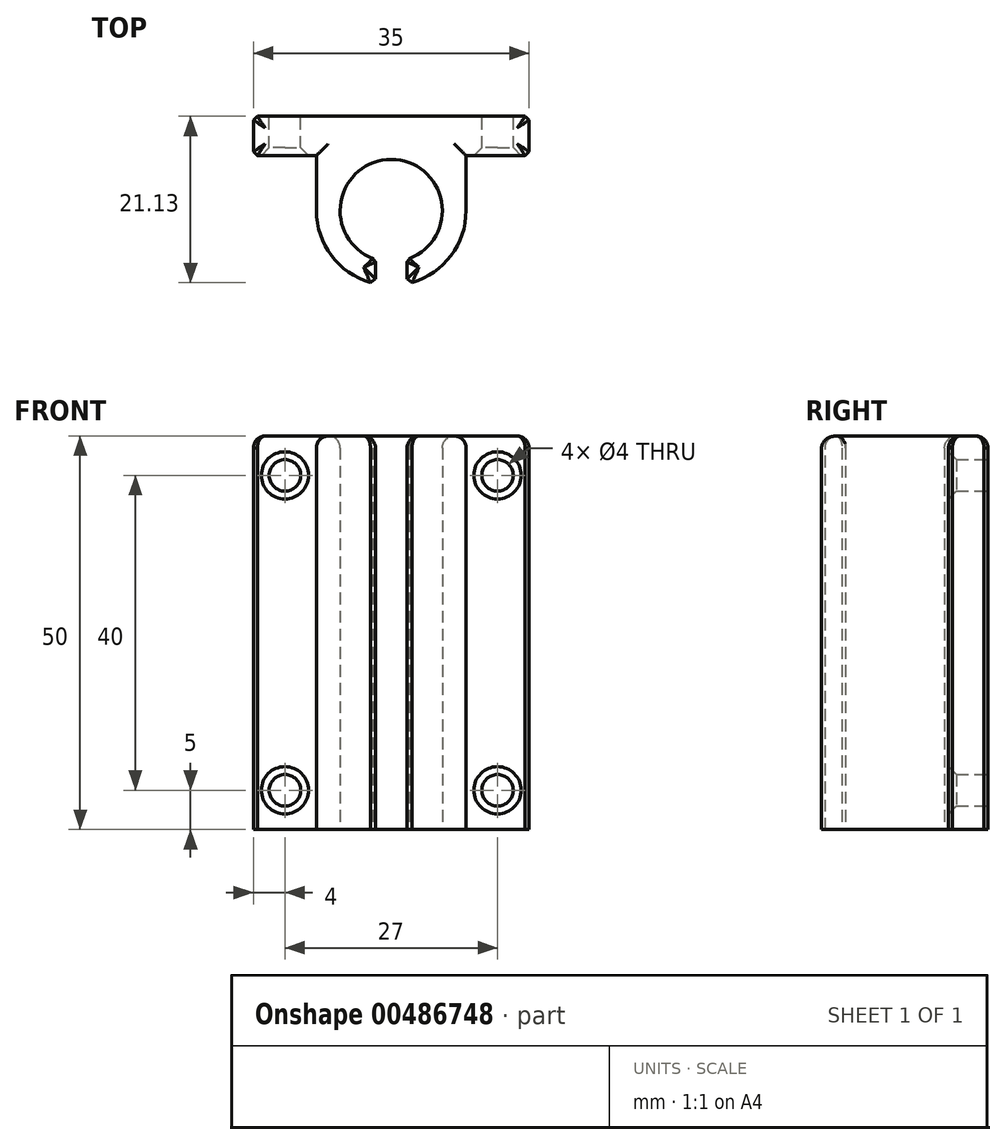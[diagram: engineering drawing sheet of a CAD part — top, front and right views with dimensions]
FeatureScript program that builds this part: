
annotation { "Feature Type Name" : "Feature", "Feature Type Description" : "" }
export const myFeature = defineFeature(function(context is Context, id is Id, definition is map)
    precondition{}
    {
        {
            var Q0;
            Q0=qCreatedBy(makeId("Top.planeOp"),FACE);
            var sketch = newSketch(context, id + "F0", { "sketchPlane" : qUnion([Q0])});
            skArc(sketch, "E0", {"start": v(2, -6.18) * mm, "mid": v(0, 6.5) * mm, "end": v(-2, -6.18) * mm});
            skArc(sketch, "E1", {"start": v(2, -9.29) * mm, "mid": v(7.4, -5.97) * mm, "end": v(9.5, 0) * mm});
            skLineSegment(sketch, "E2.0", {"start": v(-2, -6.18) * mm, "end": v(-2, -9.29) * mm});
            skLineSegment(sketch, "E3.0", {"start": v(2, -6.18) * mm, "end": v(2, -9.29) * mm});
            skLineSegment(sketch, "E4.bottom", {"start": v(17.5, 12) * mm, "end": v(-17.5, 12) * mm});
            skLineSegment(sketch, "E4.top", {"start": v(17.5, 7) * mm, "end": v(-17.5, 7) * mm});
            skLineSegment(sketch, "E4.left", {"start": v(17.5, 12) * mm, "end": v(17.5, 7) * mm});
            skLineSegment(sketch, "E4.right", {"start": v(-17.5, 12) * mm, "end": v(-17.5, 7) * mm});
            skPoint(sketch, "E4.middle", {"position": v(0, 9.5) * mm});
            skLineSegment(sketch, "E5", {"start": v(-9.5, 0) * mm, "end": v(-9.5, 7) * mm});
            skLineSegment(sketch, "E6", {"start": v(9.5, 0) * mm, "end": v(9.5, 7) * mm});
            skArc(sketch, "E7.trimOffspring", {"start": v(-9.5, 0) * mm, "mid": v(-7.4, -5.97) * mm, "end": v(-2, -9.29) * mm});
            skSolve(sketch);
        }
        {
            var Q0;
            Q0=makeQuery(id+"F0.imprint","IMPRINT",FACE,{"disambiguationData":[TD([[makeQuery(id+"F0.imprint","IMPRINT",EDGE,{"derivedFrom":sQuery(id+"F0.wireOp",EDGE,"E0")}),-1.0]])]});
            var Q1;
            Q1=makeQuery(id+"F0.imprint","IMPRINT",FACE,{"disambiguationData":[TD([[makeQuery(id+"F0.imprint","IMPRINT",EDGE,{"derivedFrom":sQuery(id+"F0.wireOp",EDGE,"E4.bottom")}),1.0]])]});
            extrude(context, id + "F1", {"entities" : qUnion([Q0, Q1]), "depth" : 50 * mm});
        }
        {
            var Q0;
            Q0=makeQuery(id+"F1.opExtrude","SWEPT_FACE",FACE,{"disambiguationData":[OSD([sQuery(id+"F0.wireOp",EDGE,"E4.bottom")])]});
            var sketch = newSketch(context, id + "F2", { "sketchPlane" : qUnion([Q0])});
            skCircle(sketch, "E8", {"center": v(13.5, 45) * mm, "radius": 2 * mm});
            skLineSegment(sketch, "E9", {"start": v(0, 50) * mm, "end": v(0, 0) * mm, "construction": true});
            skLineSegment(sketch, "E10", {"start": v(17.5, 25) * mm, "end": v(-17.5, 25) * mm, "construction": true});
            skCircle(sketch, "E11.MirrorC", {"center": v(-13.5, 45) * mm, "radius": 2 * mm});
            skCircle(sketch, "E12.MirrorC", {"center": v(-13.5, 5) * mm, "radius": 2 * mm});
            skCircle(sketch, "E13.MirrorC", {"center": v(13.5, 5) * mm, "radius": 2 * mm});
            skSolve(sketch);
        }
        {
            var Q0;
            Q0 = qSketchRegion(id + "F2", true);
            extrude(context, id + "F3", {"entities" : qUnion([Q0]), "operationType" : NewBodyOperationType.REMOVE, "endBound" : BoundingType.THROUGH_ALL, "oppositeDirection" : true, "depth" : 25 * mm});
        }
        {
            var Q0;
            {var subQ0=sQuery(id+"F0.wireOp",EDGE,"E4.top");Q0=makeQuery(id+"F3.boolean.opBoolean","INTERSECT",EDGE,{"derivedFrom":[makeQuery(id+"F1.opExtrude","SWEPT_FACE",FACE,{"disambiguationData":[OSD([subQ0]),TDD([makeQuery(id+"F0.imprint","IMPRINT",EDGE,{"disambiguationData":[TD([[makeQuery(id+"F0.imprint","INTERSECT",VERTEX,{"derivedFrom":[subQ0,sQuery(id+"F0.wireOp",EDGE,"E4.right")]}),1.0]])],"derivedFrom":subQ0})])]}),makeQuery(id+"F3.opExtrude","SWEPT_FACE",FACE,{"disambiguationData":[OSD([sQuery(id+"F2.wireOp",EDGE,"E8")])]})]});}
            var Q1;
            {var subQ0=sQuery(id+"F0.wireOp",EDGE,"E4.top");Q1=makeQuery(id+"F3.boolean.opBoolean","INTERSECT",EDGE,{"derivedFrom":[makeQuery(id+"F1.opExtrude","SWEPT_FACE",FACE,{"disambiguationData":[OSD([subQ0]),TDD([makeQuery(id+"F0.imprint","IMPRINT",EDGE,{"disambiguationData":[TD([[makeQuery(id+"F0.imprint","INTERSECT",VERTEX,{"derivedFrom":[subQ0,sQuery(id+"F0.wireOp",EDGE,"E4.left")]}),-1.0]])],"derivedFrom":subQ0})])]}),makeQuery(id+"F3.opExtrude","SWEPT_FACE",FACE,{"disambiguationData":[OSD([sQuery(id+"F2.wireOp",EDGE,"E11.MirrorC")])]})]});}
            var Q2;
            {var subQ0=sQuery(id+"F0.wireOp",EDGE,"E4.top");Q2=makeQuery(id+"F3.boolean.opBoolean","INTERSECT",EDGE,{"derivedFrom":[makeQuery(id+"F1.opExtrude","SWEPT_FACE",FACE,{"disambiguationData":[OSD([subQ0]),TDD([makeQuery(id+"F0.imprint","IMPRINT",EDGE,{"disambiguationData":[TD([[makeQuery(id+"F0.imprint","INTERSECT",VERTEX,{"derivedFrom":[subQ0,sQuery(id+"F0.wireOp",EDGE,"E4.left")]}),-1.0]])],"derivedFrom":subQ0})])]}),makeQuery(id+"F3.opExtrude","SWEPT_FACE",FACE,{"disambiguationData":[OSD([sQuery(id+"F2.wireOp",EDGE,"E12.MirrorC")])]})]});}
            var Q3;
            {var subQ0=sQuery(id+"F0.wireOp",EDGE,"E4.top");Q3=makeQuery(id+"F3.boolean.opBoolean","INTERSECT",EDGE,{"derivedFrom":[makeQuery(id+"F1.opExtrude","SWEPT_FACE",FACE,{"disambiguationData":[OSD([subQ0]),TDD([makeQuery(id+"F0.imprint","IMPRINT",EDGE,{"disambiguationData":[TD([[makeQuery(id+"F0.imprint","INTERSECT",VERTEX,{"derivedFrom":[subQ0,sQuery(id+"F0.wireOp",EDGE,"E4.right")]}),1.0]])],"derivedFrom":subQ0})])]}),makeQuery(id+"F3.opExtrude","SWEPT_FACE",FACE,{"disambiguationData":[OSD([sQuery(id+"F2.wireOp",EDGE,"E13.MirrorC")])]})]});}
            chamfer(context, id + "F4", {"entities" : qUnion([Q0, Q1, Q2, Q3]), "width" : 1 * mm, "tangentPropagation" : true});
        }
        {
            var Q0;
            Q0=makeQuery(id+"F1.opExtrude","CAP_FACE",FACE,{"disambiguationData":[OSD([sQuery(id+"F0.wireOp",EDGE,"E0"),sQuery(id+"F0.wireOp",EDGE,"E1"),sQuery(id+"F0.wireOp",EDGE,"E2.0"),sQuery(id+"F0.wireOp",EDGE,"E3.0"),sQuery(id+"F0.wireOp",EDGE,"E4.bottom"),sQuery(id+"F0.wireOp",EDGE,"E4.top"),sQuery(id+"F0.wireOp",EDGE,"E4.left"),sQuery(id+"F0.wireOp",EDGE,"E4.right"),sQuery(id+"F0.wireOp",EDGE,"E5"),sQuery(id+"F0.wireOp",EDGE,"E6"),sQuery(id+"F0.wireOp",EDGE,"E7.trimOffspring")])],"isStart":false});
            fillet(context, id + "F5", {"entities" : qUnion([Q0]), "radius" : 1.5 * mm, "tangentPropagation" : true, "allowEdgeOverflow" : false});
        }
        {
            var Q0;
            Q0=makeQuery(id+"F1.opExtrude","SWEPT_EDGE",EDGE,{"disambiguationData":[OSD([sQuery(id+"F0.wireOp",EDGE,"E4.bottom"),sQuery(id+"F0.wireOp",EDGE,"E4.left")])]});
            var Q1;
            Q1=makeQuery(id+"F1.opExtrude","SWEPT_EDGE",EDGE,{"disambiguationData":[OSD([sQuery(id+"F0.wireOp",EDGE,"E4.top"),sQuery(id+"F0.wireOp",EDGE,"E4.left")])]});
            var Q2;
            Q2=makeQuery(id+"F1.opExtrude","SWEPT_EDGE",EDGE,{"disambiguationData":[OSD([sQuery(id+"F0.wireOp",EDGE,"E2.0"),sQuery(id+"F0.wireOp",EDGE,"E7.trimOffspring")])]});
            var Q3;
            Q3=makeQuery(id+"F1.opExtrude","SWEPT_EDGE",EDGE,{"disambiguationData":[OSD([sQuery(id+"F0.wireOp",EDGE,"E1"),sQuery(id+"F0.wireOp",EDGE,"E3.0")])]});
            var Q4;
            Q4=makeQuery(id+"F1.opExtrude","SWEPT_EDGE",EDGE,{"disambiguationData":[OSD([sQuery(id+"F0.wireOp",EDGE,"E0"),sQuery(id+"F0.wireOp",EDGE,"E3.0")])]});
            var Q5;
            Q5=makeQuery(id+"F1.opExtrude","SWEPT_EDGE",EDGE,{"disambiguationData":[OSD([sQuery(id+"F0.wireOp",EDGE,"E0"),sQuery(id+"F0.wireOp",EDGE,"E2.0")])]});
            var Q6;
            Q6=makeQuery(id+"F1.opExtrude","SWEPT_EDGE",EDGE,{"disambiguationData":[OSD([sQuery(id+"F0.wireOp",EDGE,"E4.bottom"),sQuery(id+"F0.wireOp",EDGE,"E4.right")])]});
            var Q7;
            Q7=makeQuery(id+"F1.opExtrude","SWEPT_EDGE",EDGE,{"disambiguationData":[OSD([sQuery(id+"F0.wireOp",EDGE,"E4.top"),sQuery(id+"F0.wireOp",EDGE,"E4.right")])]});
            chamfer(context, id + "F6", {"entities" : qUnion([Q0, Q1, Q2, Q3, Q4, Q5, Q6, Q7]), "width" : 0.5 * mm, "tangentPropagation" : true});
        }
    });
